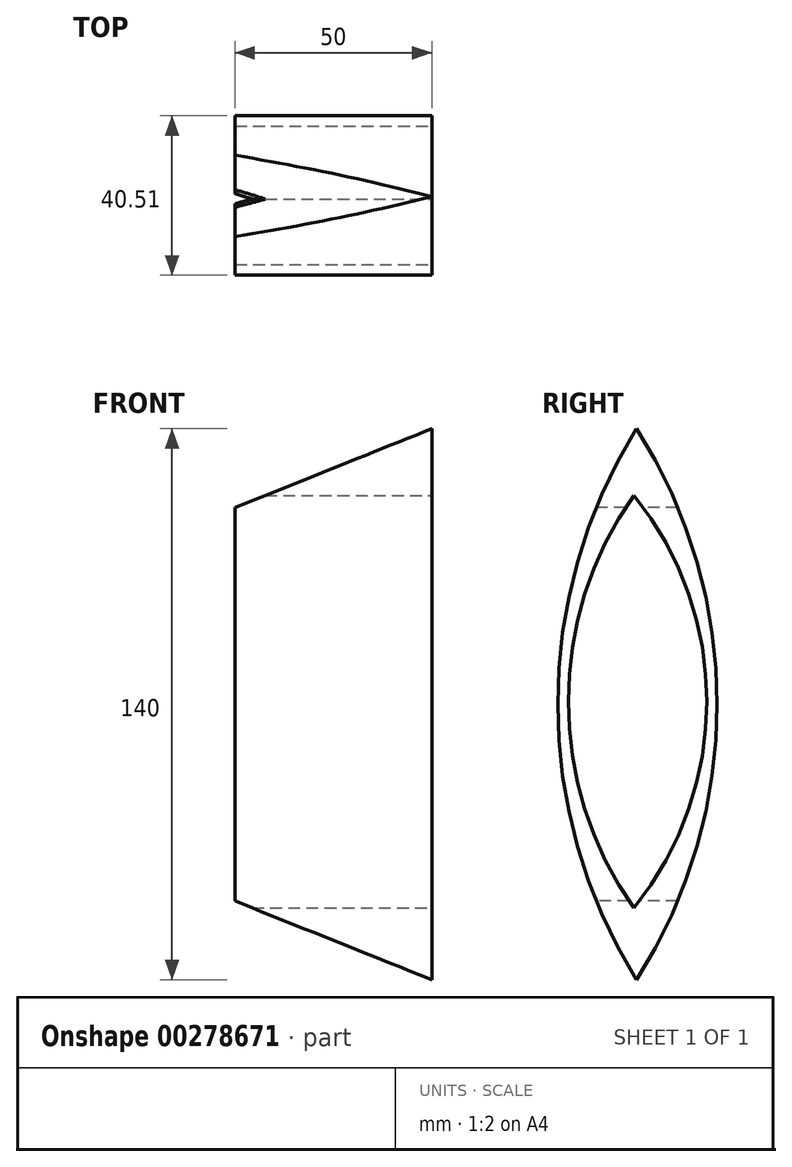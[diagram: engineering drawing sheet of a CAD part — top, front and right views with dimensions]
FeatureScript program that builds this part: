
annotation { "Feature Type Name" : "Feature", "Feature Type Description" : "" }
export const myFeature = defineFeature(function(context is Context, id is Id, definition is map)
    precondition{}
    {
        {
            var Q0;
            Q0=qCreatedBy(makeId("Front.planeOp"),FACE);
            var sketch = newSketch(context, id + "F0", { "sketchPlane" : qUnion([Q0])});
            skLineSegment(sketch, "E0.bottom", {"start": v(-25, 70) * mm, "end": v(25, 70) * mm});
            skLineSegment(sketch, "E0.top", {"start": v(-25, -70) * mm, "end": v(25, -70) * mm});
            skLineSegment(sketch, "E0.left", {"start": v(-25, 70) * mm, "end": v(-25, -70) * mm});
            skLineSegment(sketch, "E0.right", {"start": v(25, 70) * mm, "end": v(25, -70) * mm});
            skSolve(sketch);
        }
        {
            var Q0;
            Q0 = qSketchRegion(id + "F0", true);
            extrude(context, id + "F1", {"entities" : qUnion([Q0]), "depth" : 42 * mm, "offsetDistance" : 25 * mm});
        }
        {
            var Q0;
            Q0=makeQuery(id+"F1.opExtrude","CAP_FACE",FACE,{"disambiguationData":[OSD([sQuery(id+"F0.wireOp",EDGE,"E0.bottom"),sQuery(id+"F0.wireOp",EDGE,"E0.top"),sQuery(id+"F0.wireOp",EDGE,"E0.left"),sQuery(id+"F0.wireOp",EDGE,"E0.right")])],"isStart":false});
            var sketch = newSketch(context, id + "F2", { "sketchPlane" : qUnion([Q0])});
            skLineSegment(sketch, "E1", {"start": v(-25, 70) * mm, "end": v(-25, 50) * mm});
            skLineSegment(sketch, "E2", {"start": v(-25, 50) * mm, "end": v(25, 70) * mm});
            skLineSegment(sketch, "E3", {"start": v(25, 70) * mm, "end": v(-25, 70) * mm});
            skLineSegment(sketch, "E4", {"start": v(-25, -70) * mm, "end": v(-25, -50) * mm});
            skLineSegment(sketch, "E5", {"start": v(-25, -50) * mm, "end": v(25, -70) * mm});
            skLineSegment(sketch, "E6", {"start": v(25, -70) * mm, "end": v(-25, -70) * mm});
            skSolve(sketch);
        }
        {
            var Q0;
            Q0 = qSketchRegion(id + "F2", true);
            extrude(context, id + "F3", {"entities" : qUnion([Q0]), "operationType" : NewBodyOperationType.REMOVE, "oppositeDirection" : true, "depth" : 42 * mm, "offsetDistance" : 25 * mm});
        }
        {
            var Q0;
            Q0=makeQuery(id+"F1.opExtrude","SWEPT_FACE",FACE,{"disambiguationData":[OSD([sQuery(id+"F0.wireOp",EDGE,"E0.right")])]});
            var sketch = newSketch(context, id + "F4", { "sketchPlane" : qUnion([Q0])});
            skLineSegment(sketch, "E7", {"start": v(-21, 70) * mm, "end": v(-47.73, 70) * mm});
            skLineSegment(sketch, "E8", {"start": v(-47.73, 70) * mm, "end": v(-47.73, -70) * mm});
            skLineSegment(sketch, "E9", {"start": v(-47.73, -70) * mm, "end": v(-21, -70) * mm});
            skArc(sketch, "E10", {"start": v(-21, 70) * mm, "mid": v(-40.97, 0) * mm, "end": v(-21, -70) * mm});
            skSolve(sketch);
        }
        {
            var Q0;
            Q0 = qSketchRegion(id + "F4", true);
            extrude(context, id + "F5", {"entities" : qUnion([Q0]), "operationType" : NewBodyOperationType.REMOVE, "oppositeDirection" : true, "depth" : 50 * mm, "offsetDistance" : 25 * mm});
        }
        {
            var Q0;
            Q0=makeQuery(id+"F1.opExtrude","SWEPT_FACE",FACE,{"disambiguationData":[OSD([sQuery(id+"F0.wireOp",EDGE,"E0.right")])]});
            var sketch = newSketch(context, id + "F6", { "sketchPlane" : qUnion([Q0])});
            skArc(sketch, "E11", {"start": v(-21, -70) * mm, "mid": v(-0.46, 0) * mm, "end": v(-21, 70) * mm});
            skLineSegment(sketch, "E12", {"start": v(-21, 70) * mm, "end": v(3.54, 70) * mm});
            skLineSegment(sketch, "E13", {"start": v(3.54, 70) * mm, "end": v(3.54, -70) * mm});
            skLineSegment(sketch, "E14", {"start": v(3.54, -70) * mm, "end": v(-21, -70) * mm});
            skSolve(sketch);
        }
        {
            var Q0;
            Q0 = qSketchRegion(id + "F6", true);
            extrude(context, id + "F7", {"entities" : qUnion([Q0]), "operationType" : NewBodyOperationType.REMOVE, "oppositeDirection" : true, "depth" : 50 * mm, "offsetDistance" : 25 * mm});
        }
        {
            var Q0;
            Q0=makeQuery(id+"F1.opExtrude","SWEPT_FACE",FACE,{"disambiguationData":[OSD([sQuery(id+"F0.wireOp",EDGE,"E0.right")])]});
            var sketch = newSketch(context, id + "F8", { "sketchPlane" : qUnion([Q0])});
            skPoint(sketch, "E15.start.orphan", {"position": v(-21.61, 58.02) * mm});
            skArc(sketch, "E16", {"start": v(-21.61, -51.74) * mm, "mid": v(-3.1, 0.67) * mm, "end": v(-21.61, 53.07) * mm});
            skArc(sketch, "E17", {"start": v(-21.61, 53.07) * mm, "mid": v(-38.3, 0.67) * mm, "end": v(-21.61, -51.74) * mm});
            skSolve(sketch);
        }
        {
            var Q0;
            Q0 = qSketchRegion(id + "F8", true);
            extrude(context, id + "F9", {"entities" : qUnion([Q0]), "operationType" : NewBodyOperationType.REMOVE, "oppositeDirection" : true, "depth" : 50 * mm, "offsetDistance" : 25 * mm});
        }
    });
